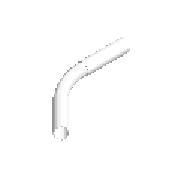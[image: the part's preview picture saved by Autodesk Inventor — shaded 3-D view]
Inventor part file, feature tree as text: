
AUTODESK INVENTOR PART (.ipt)
format: ipt  version: 2023 (Build 270158000, 158)  size: 200,704 bytes
history: native  units: mm (DEFAULTED — no unit token found)
features: other x6, sketch x2, revolve x2, sweep x1
ambient origin geometry x8: Origin, YZ Plane, XZ Plane, XY Plane, X Axis, Y Axis, Z Axis, Center Point
bodies: Solid1 (feature_tree)
feature tree (11):
  sketch  "Sketch1"  dims[d0=182.0mm d1=91.0mm]
  revolve  "Revolve1"  [1 undecoded]
  revolve  "Revolve2"  [1 undecoded]
  sketch  "Sketch2"  dims[d2=93.6mm d3=110.0mm d4=126.4mm d5=203.0mm d6=203.0mm d7=182.0mm d8=91.0mm d9=93.6mm d10=110.0mm d11=126.4mm d36=90.0deg d37=90.0deg d12=45.0deg d13=0.0mm d40=0.0mm]
  sweep  "Sweep1"
  other  "Work Point3"
  other  "Work Point4"
  other  "Work Axis2"
  other  "Work Point5"
  other  "Work Axis3"
  other  "Work Point6"
note: 2 required parameter values undecoded (feature->parameter linkage not recoverable at this tier; creation-order binding heuristic only, values carry confidence <= 0.55)
